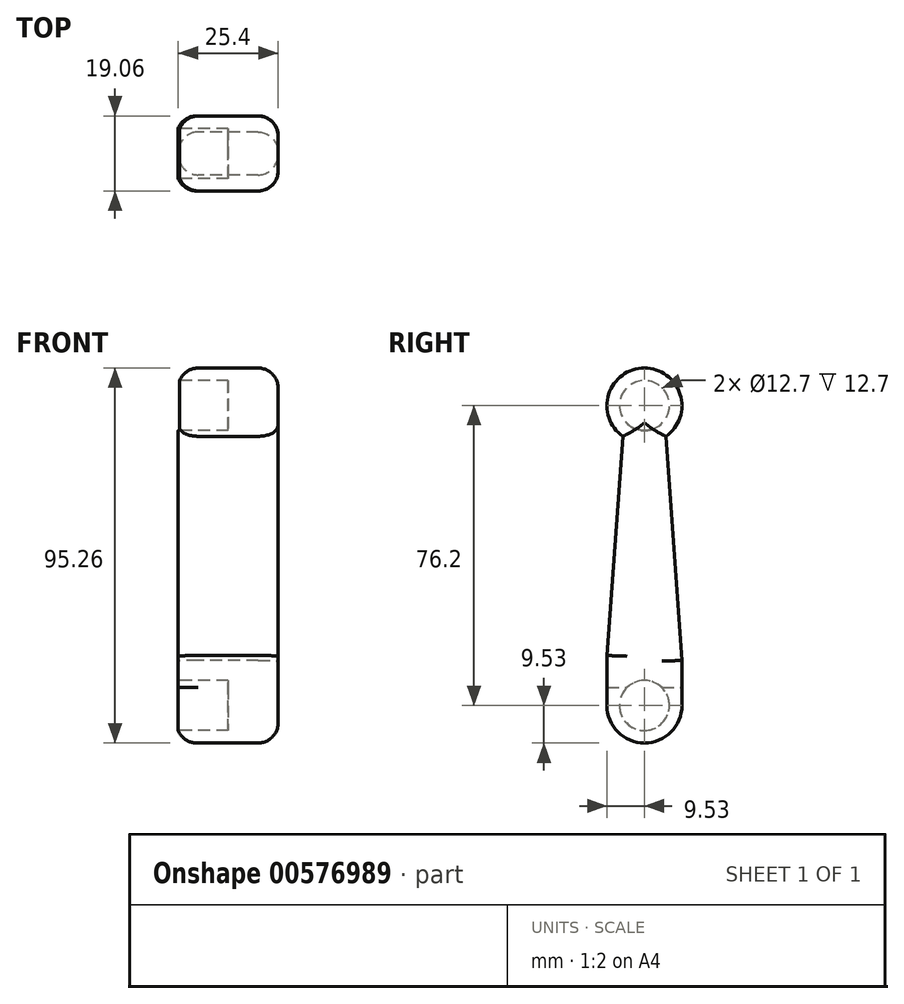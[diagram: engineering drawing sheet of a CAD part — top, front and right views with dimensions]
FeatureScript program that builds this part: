
annotation { "Feature Type Name" : "Feature", "Feature Type Description" : "" }
export const myFeature = defineFeature(function(context is Context, id is Id, definition is map)
    precondition{}
    {
        {
            var Q0;
            Q0=qCreatedBy(makeId("Right.planeOp"),FACE);
            var sketch = newSketch(context, id + "F0", { "sketchPlane" : qUnion([Q0])});
            skCircle(sketch, "E0", {"center": v(0, 0) * mm, "radius": 6.35 * mm});
            skArc(sketch, "E1", {"start": v(-9.53, 0) * mm, "mid": v(0, -9.53) * mm, "end": v(9.53, 0) * mm});
            skLineSegment(sketch, "E2", {"start": v(-9.53, 0) * mm, "end": v(-9.53, 12.7) * mm});
            skLineSegment(sketch, "E3", {"start": v(-9.52, 12.7) * mm, "end": v(-5.46, 68.4) * mm});
            skLineSegment(sketch, "E4.MirrorCS", {"start": v(9.52, 11.44) * mm, "end": v(5.46, 68.4) * mm});
            skLineSegment(sketch, "E5.MirrorCS", {"start": v(9.53, 0) * mm, "end": v(9.53, 12.7) * mm});
            skArc(sketch, "E6", {"start": v(5.46, 68.4) * mm, "mid": v(0, 85.73) * mm, "end": v(-5.46, 68.4) * mm});
            skCircle(sketch, "E7", {"center": v(0, 76.2) * mm, "radius": 6.35 * mm});
            skPoint(sketch, "E8.orphan", {"position": v(-6.66, 51.94) * mm});
            skPoint(sketch, "E9.orphan", {"position": v(6.63, 51.94) * mm});
            skSolve(sketch);
        }
        {
            var Q0;
            Q0=makeQuery(id+"F0.imprint","IMPRINT",FACE,{"disambiguationData":[TD([[makeQuery(id+"F0.imprint","IMPRINT",EDGE,{"derivedFrom":sQuery(id+"F0.wireOp",EDGE,"E0")}),-1.0]])]});
            extrude(context, id + "F1", {"entities" : qUnion([Q0]), "depth" : 25.4 * mm, "offsetDistance" : 25.4 * mm});
        }
        {
            var Q0;
            Q0=makeQuery(id+"F1.opExtrude","CAP_FACE",FACE,{"disambiguationData":[OSD([sQuery(id+"F0.wireOp",EDGE,"E0"),sQuery(id+"F0.wireOp",EDGE,"E1"),sQuery(id+"F0.wireOp",EDGE,"E2"),sQuery(id+"F0.wireOp",EDGE,"E3"),sQuery(id+"F0.wireOp",EDGE,"E4.MirrorCS"),sQuery(id+"F0.wireOp",EDGE,"E5.MirrorCS"),sQuery(id+"F0.wireOp",EDGE,"E6"),sQuery(id+"F0.wireOp",EDGE,"E7")])],"isStart":false});
            var sketch = newSketch(context, id + "F2", { "sketchPlane" : qUnion([Q0])});
            skCircle(sketch, "E10", {"center": v(0, 76.2) * mm, "radius": 6.35 * mm});
            skCircle(sketch, "E11", {"center": v(0, 0) * mm, "radius": 6.35 * mm});
            skSolve(sketch);
        }
        {
            var Q0;
            Q0=makeQuery(id+"F2.imprint","IMPRINT",FACE,{"disambiguationData":[TD([[makeQuery(id+"F2.imprint","IMPRINT",EDGE,{"derivedFrom":sQuery(id+"F2.wireOp",EDGE,"E10")}),1.0]])]});
            var Q1;
            Q1=makeQuery(id+"F2.imprint","IMPRINT",FACE,{"disambiguationData":[TD([[makeQuery(id+"F2.imprint","IMPRINT",EDGE,{"derivedFrom":sQuery(id+"F2.wireOp",EDGE,"E11")}),1.0]])]});
            extrude(context, id + "F3", {"entities" : qUnion([Q0, Q1]), "operationType" : NewBodyOperationType.ADD, "oppositeDirection" : true, "depth" : 12.7 * mm, "offsetDistance" : 25.4 * mm});
        }
        {
            var Q0;
            Q0=makeQuery(id+"F1.opExtrude","CAP_EDGE",EDGE,{"disambiguationData":[OSD([sQuery(id+"F0.wireOp",EDGE,"E3")])],"isStart":true});
            var Q1;
            Q1=makeQuery(id+"F1.opExtrude","CAP_EDGE",EDGE,{"disambiguationData":[OSD([sQuery(id+"F0.wireOp",EDGE,"E4.MirrorCS")])],"isStart":true});
            var Q2;
            Q2=makeQuery(id+"F1.opExtrude","CAP_EDGE",EDGE,{"disambiguationData":[OSD([sQuery(id+"F0.wireOp",EDGE,"E6")])],"isStart":true});
            var Q3;
            Q3=makeQuery(id+"F1.opExtrude","CAP_EDGE",EDGE,{"disambiguationData":[OSD([sQuery(id+"F0.wireOp",EDGE,"E1")])],"isStart":true});
            fillet(context, id + "F4", {"entities" : qUnion([Q0, Q1, Q2, Q3]), "radius" : 5.08 * mm, "tangentPropagation" : true, "allowEdgeOverflow" : false});
        }
        {
            var Q0;
            Q0=makeQuery(id+"F1.opExtrude","CAP_EDGE",EDGE,{"disambiguationData":[OSD([sQuery(id+"F0.wireOp",EDGE,"E6")])],"isStart":false});
            var Q1;
            Q1=makeQuery(id+"F1.opExtrude","CAP_EDGE",EDGE,{"disambiguationData":[OSD([sQuery(id+"F0.wireOp",EDGE,"E3")])],"isStart":false});
            var Q2;
            Q2=makeQuery(id+"F1.opExtrude","CAP_EDGE",EDGE,{"disambiguationData":[OSD([sQuery(id+"F0.wireOp",EDGE,"E2")])],"isStart":false});
            var Q3;
            Q3=makeQuery(id+"F1.opExtrude","CAP_EDGE",EDGE,{"disambiguationData":[OSD([sQuery(id+"F0.wireOp",EDGE,"E1")])],"isStart":false});
            var Q4;
            Q4=makeQuery(id+"F1.opExtrude","CAP_EDGE",EDGE,{"disambiguationData":[OSD([sQuery(id+"F0.wireOp",EDGE,"E4.MirrorCS")])],"isStart":false});
            var Q5;
            Q5=makeQuery(id+"F1.opExtrude","CAP_EDGE",EDGE,{"disambiguationData":[OSD([sQuery(id+"F0.wireOp",EDGE,"E5.MirrorCS")])],"isStart":false});
            fillet(context, id + "F5", {"entities" : qUnion([Q0, Q1, Q2, Q3, Q4, Q5]), "radius" : 5.08 * mm, "tangentPropagation" : true, "allowEdgeOverflow" : false});
        }
    });
